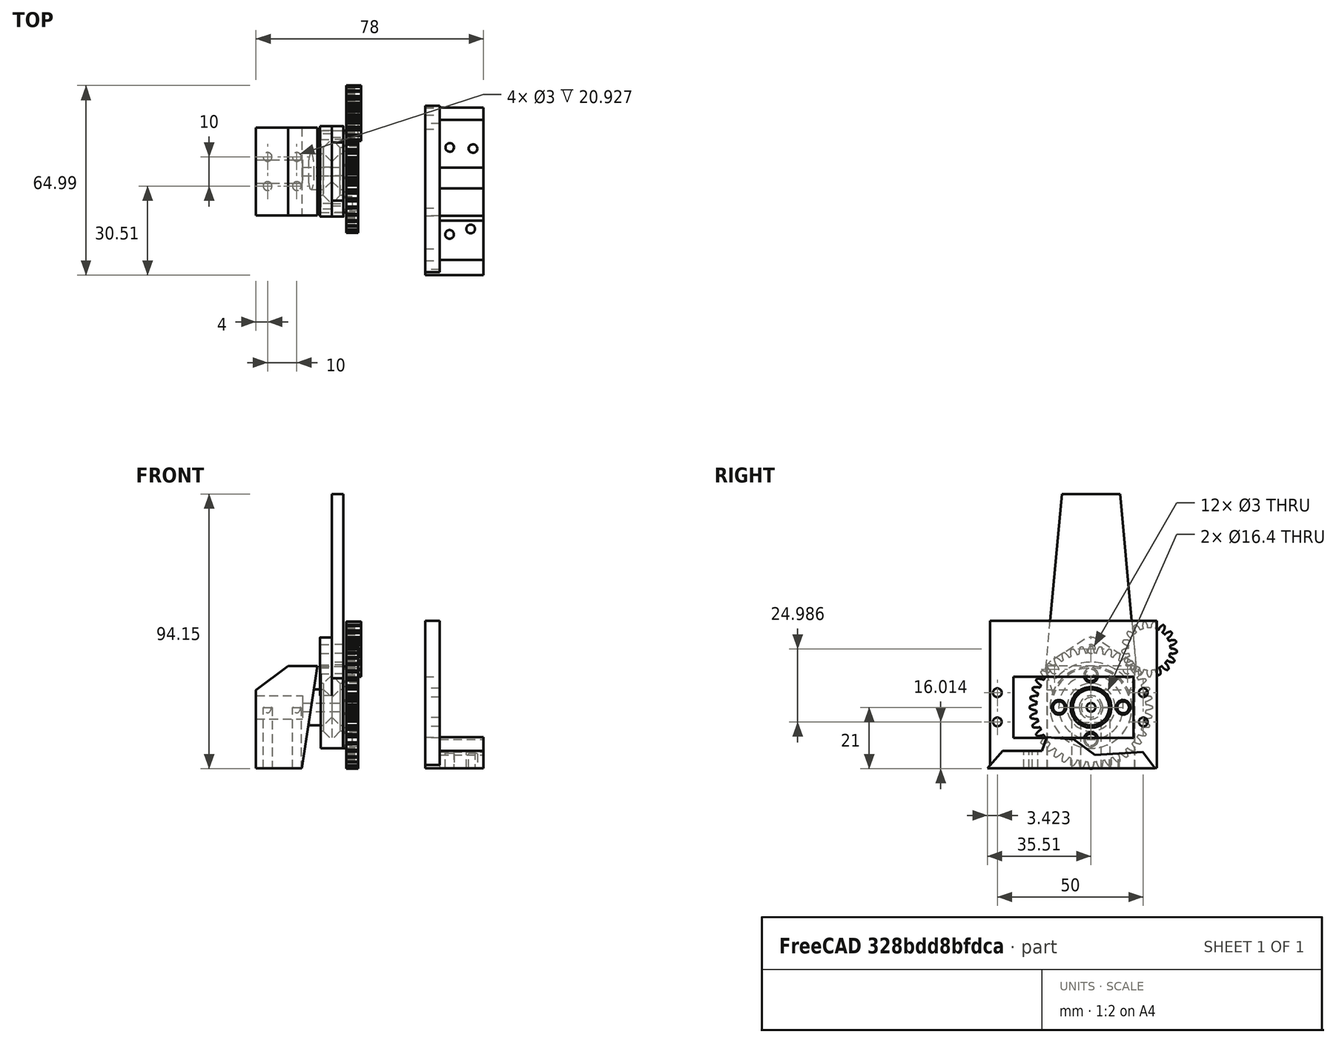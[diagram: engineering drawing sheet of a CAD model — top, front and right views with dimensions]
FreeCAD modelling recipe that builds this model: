
FCSTD DOCUMENT  (FreeCAD 0.16RUnknown)
Label: ArmV2
License: All rights reserved
LicenseURL: http://en.wikipedia.org/wiki/All_rights_reserved
objects: Sketcher::SketchObject×15, PartDesign::Pad×10, Part::Cut×5, PartDesign::Revolution×4, Part::MultiFuse×3, Part::FeaturePython×2, Mesh::Feature×2, Part::Cylinder×1
note: 54 computed .brp shape members not serialized (recipe doc carries the construction recipe); baked Part::Feature solids carry a one-line shape summary decoded from their .brp

FEATURE [Sketcher::SketchObject] Sketch
  Placement = pos=(0,0,0) rot=(-1,0,0;4.71239rad)
  sketch-geometry (22):
    g0: Circle [constr] CenterX=0 CenterY=7.20025 CenterZ=0 NormalX=0 NormalY=0 NormalZ=1 Radius=2.225
    g1: Circle [constr] CenterX=4.2322 CenterY=5.82513 CenterZ=0 NormalX=0 NormalY=0 NormalZ=1 Radius=2.225
    g2: Circle [constr] CenterX=0 CenterY=0 CenterZ=0 NormalX=0 NormalY=0 NormalZ=1 Radius=7.20025
    g3: LineSegment [constr] StartX=4.2322 StartY=5.82513 StartZ=0 EndX=0 EndY=0 EndZ=0
    g4: LineSegment StartX=0 StartY=11.054 StartZ=0 EndX=-2.85373 EndY=8.20025 EndZ=0
    g5: LineSegment StartX=-2.85373 StartY=8.20025 StartZ=0 EndX=-3.85373 EndY=8.20025 EndZ=0
    g6: LineSegment StartX=-3.85373 StartY=8.20025 StartZ=0 EndX=-3.85373 EndY=14.054 EndZ=0
    g7: LineSegment StartX=-3.85373 StartY=14.054 StartZ=0 EndX=3.85373 EndY=14.054 EndZ=0
    g8: LineSegment StartX=3.85373 StartY=14.054 StartZ=0 EndX=3.85373 EndY=8.20025 EndZ=0
    g9: LineSegment StartX=3.85373 StartY=8.20025 StartZ=0 EndX=2.85373 EndY=8.20025 EndZ=0
    g10: LineSegment StartX=2.85373 StartY=8.20025 StartZ=0 EndX=0 EndY=11.054 EndZ=0
    g11: Circle [constr] CenterX=0 CenterY=7.20025 CenterZ=0 NormalX=0 NormalY=0 NormalZ=1 Radius=2.725
    g12: LineSegment [constr] StartX=0 StartY=7.20025 StartZ=0 EndX=0 EndY=4.97525 EndZ=0
    g13: LineSegment [constr] StartX=0 StartY=4.97525 StartZ=0 EndX=0 EndY=4.47525 EndZ=0
    g14: GeomPoint [constr] X=0 Y=14.054 Z=0
    g15: LineSegment [constr] StartX=-3.85373 StartY=6.20025 StartZ=0 EndX=-2.85373 EndY=6.20025 EndZ=0
    g16: LineSegment [constr] StartX=-2.85373 StartY=6.20025 StartZ=0 EndX=0 EndY=3.34652 EndZ=0
    g17: LineSegment [constr] StartX=0 StartY=3.34652 StartZ=0 EndX=2.85373 EndY=6.20025 EndZ=0
    g18: LineSegment [constr] StartX=2.85373 StartY=6.20025 StartZ=0 EndX=3.85373 EndY=6.20025 EndZ=0
    g19: LineSegment [constr] StartX=3.85373 StartY=6.20025 StartZ=0 EndX=3.85373 EndY=0 EndZ=0
    g20: LineSegment [constr] StartX=3.85373 StartY=0 StartZ=0 EndX=-3.85373 EndY=0 EndZ=0
    g21: LineSegment [constr] StartX=-3.85373 StartY=0 StartZ=0 EndX=-3.85373 EndY=6.20025 EndZ=0
  constraints (62):
    c: PointOnObject(g0,g-2)
    c: Coincident(g2,g-1)
    c: PointOnObject(g0,g2)
    c: PointOnObject(g1,g2)
    c: Tangent(g0,g1)
    c: Equal(g1,g0)
    c: Radius(g0) = 2.225
    c: Coincident(g3,g1)
    c: Coincident(g3,g-1)
    c: Angle(g3,g-2) = 0.628319
    c: PointOnObject(g4,g-2)
    c: Coincident(g4,g5)
    c: Horizontal(g5)
    c: Coincident(g5,g6)
    c: Vertical(g6)
    c: Coincident(g6,g7)
    c: Horizontal(g7)
    c: Coincident(g7,g8)
    c: Vertical(g8)
    c: Coincident(g8,g9)
    c: Horizontal(g9)
    c: Coincident(g9,g10)
    c: Coincident(g10,g4)
    c: Coincident(g11,g0)
    c: Coincident(g12,g0)
    c: Coincident(g12,g13)
    c: PointOnObject(g12,g0)
    c: PointOnObject(g13,g11)
    c: Parallel(g13,g12)
    c: Distance(g13) = 0.5
    c: Tangent(g11,g4)
    c: Tangent(g10,g11)
    c: Equal(g4,g10)
    c: Equal(g9,g5)
    c: PointOnObject(g14,g7)
    c: PointOnObject(g14,g-2)
    c: DistanceY(g4,g14) = 3
    c: DistanceY(g0,g4) = 1
    c: DistanceX(g5,g5) = 1
    c: Angle(g4,g10) = 1.5708
    c: PointOnObject(g13,g-2)
    c: Coincident(g15,g16)
    c: Coincident(g16,g17)
    c: Coincident(g17,g18)
    c: Coincident(g18,g19)
    c: Coincident(g19,g20)
    c: Horizontal(g20)
    c: Coincident(g20,g21)
    c: Coincident(g21,g15)
    c: PointOnObject(g20,g-1)
    c: Vertical(g21)
    c: Vertical(g19)
    c: Horizontal(g18)
    c: Horizontal(g15)
    c: Equal(g18,g15)
    c: Equal(g15,g5)
    c: PointOnObject(g16,g-2)
    c: Tangent(g16,g11)
    c: Tangent(g11,g17)
    c: Angle(g17,g16) = 1.5708
    c: Equal(g16,g17)
    c: DistanceY(g15,g0) = 1
FEATURE [Sketcher::SketchObject] Sketch001
  Placement = pos=(0,0,0) rot=(1,0,0;1.5708rad)
  sketch-geometry (24):
    g0: Circle [constr] CenterX=0 CenterY=7.20025 CenterZ=0 NormalX=0 NormalY=0 NormalZ=1 Radius=2.225
    g1: Circle [constr] CenterX=4.2322 CenterY=5.82513 CenterZ=0 NormalX=0 NormalY=0 NormalZ=1 Radius=2.225
    g2: Circle [constr] CenterX=0 CenterY=0 CenterZ=0 NormalX=0 NormalY=0 NormalZ=1 Radius=7.20025
    g3: LineSegment [constr] StartX=4.2322 StartY=5.82513 StartZ=0 EndX=0 EndY=0 EndZ=0
    g4: LineSegment [constr] StartX=0 StartY=11.054 StartZ=0 EndX=-2.85373 EndY=8.20025 EndZ=0
    g5: LineSegment [constr] StartX=-2.85373 StartY=8.20025 StartZ=0 EndX=-7.85373 EndY=8.20025 EndZ=0
    g6: LineSegment [constr] StartX=-7.85373 StartY=8.20025 StartZ=0 EndX=-7.85373 EndY=14.054 EndZ=0
    g7: LineSegment [constr] StartX=-7.85373 StartY=14.054 StartZ=0 EndX=7.85373 EndY=14.054 EndZ=0
    g8: LineSegment [constr] StartX=7.85373 StartY=14.054 StartZ=0 EndX=7.85373 EndY=8.20025 EndZ=0
    g9: LineSegment [constr] StartX=7.85373 StartY=8.20025 StartZ=0 EndX=2.85373 EndY=8.20025 EndZ=0
    g10: LineSegment [constr] StartX=2.85373 StartY=8.20025 StartZ=0 EndX=0 EndY=11.054 EndZ=0
    g11: Circle [constr] CenterX=0 CenterY=7.20025 CenterZ=0 NormalX=0 NormalY=0 NormalZ=1 Radius=2.725
    g12: LineSegment [constr] StartX=0 StartY=7.20025 StartZ=0 EndX=0 EndY=4.97525 EndZ=0
    g13: LineSegment [constr] StartX=0 StartY=4.97525 StartZ=0 EndX=0 EndY=4.47525 EndZ=0
    g14: GeomPoint [constr] X=0 Y=14.054 Z=0
    g15: LineSegment StartX=-7.85373 StartY=6.20025 StartZ=0 EndX=-2.85373 EndY=6.20025 EndZ=0
    g16: LineSegment StartX=-2.85373 StartY=6.20025 StartZ=0 EndX=0 EndY=3.34652 EndZ=0
    g17: LineSegment [constr] StartX=0 StartY=3.34652 StartZ=0 EndX=2.85373 EndY=6.20025 EndZ=0
    g18: LineSegment [constr] StartX=2.85373 StartY=6.20025 StartZ=0 EndX=7.85373 EndY=6.20025 EndZ=0
    g19: LineSegment [constr] StartX=7.85373 StartY=6.20025 StartZ=0 EndX=7.85373 EndY=0 EndZ=0
    g20: LineSegment StartX=-7.85373 StartY=0 StartZ=0 EndX=-7.85373 EndY=6.20025 EndZ=0
    g21: LineSegment StartX=0 StartY=3.34652 StartZ=0 EndX=0 EndY=0 EndZ=0
    g22: LineSegment StartX=-7.85373 StartY=0 StartZ=0 EndX=0 EndY=0 EndZ=0
    g23: LineSegment [constr] StartX=0 StartY=0 StartZ=0 EndX=7.85373 EndY=0 EndZ=0
  constraints (66):
    c: PointOnObject(g0,g-2)
    c: Coincident(g2,g-1)
    c: PointOnObject(g0,g2)
    c: PointOnObject(g1,g2)
    c: Tangent(g0,g1)
    c: Equal(g1,g0)
    c: Radius(g0) = 2.225
    c: Coincident(g3,g1)
    c: Coincident(g3,g-1)
    c: Angle(g3,g-2) = 0.628319
    c: PointOnObject(g4,g-2)
    c: Coincident(g4,g5)
    c: Horizontal(g5)
    c: Coincident(g5,g6)
    c: Vertical(g6)
    c: Coincident(g6,g7)
    c: Horizontal(g7)
    c: Coincident(g7,g8)
    c: Vertical(g8)
    c: Coincident(g8,g9)
    c: Horizontal(g9)
    c: Coincident(g9,g10)
    c: Coincident(g10,g4)
    c: Coincident(g11,g0)
    c: Coincident(g12,g0)
    c: Coincident(g12,g13)
    c: PointOnObject(g12,g0)
    c: PointOnObject(g13,g11)
    c: Parallel(g13,g12)
    c: Distance(g13) = 0.5
    c: Tangent(g11,g4)
    c: Tangent(g10,g11)
    c: Equal(g4,g10)
    c: Equal(g9,g5)
    c: PointOnObject(g14,g7)
    c: PointOnObject(g14,g-2)
    c: DistanceY(g4,g14) = 3
    c: DistanceY(g0,g4) = 1
    c: DistanceX(g5,g5) = 5
    c: Angle(g4,g10) = 1.5708
    c: PointOnObject(g13,g-2)
    c: Coincident(g15,g16)
    c: Coincident(g16,g17)
    c: Coincident(g17,g18)
    c: Coincident(g18,g19)
    c: Coincident(g20,g15)
    c: PointOnObject(g20,g-1)
    c: Vertical(g20)
    c: Vertical(g19)
    c: Horizontal(g18)
    c: Horizontal(g15)
    c: Equal(g18,g15)
    c: Equal(g15,g5)
    c: PointOnObject(g16,g-2)
    c: Tangent(g16,g11)
    c: Tangent(g11,g17)
    c: Angle(g17,g16) = 1.5708
    c: Equal(g16,g17)
    c: DistanceY(g15,g0) = 1
    c: Coincident(g21,g16)
    c: Coincident(g20,g22)
    c: Coincident(g22,g21)
    c: Coincident(g22,g23)
    c: Coincident(g23,g19)
    c: Coincident(g-1,g21)
    c: PointOnObject(g19,g-1)
FEATURE [PartDesign::Revolution] Revolution  label="OuterRace"
  Angle = 360
  Axis = (1,0,0)
  Base = (0,0,0)
  Placement = pos=(0,0,0) rot=(-1,0,0;4.71239rad)
  ReferenceAxis = -> Sketch [H_Axis]
  Sketch = -> Sketch
FEATURE [PartDesign::Revolution] Revolution001  label="InnerRace002"
  Angle = 360
  Axis = (1,0,0)
  Base = (0,0,0)
  Placement = pos=(0,0,0) rot=(1,0,0;1.5708rad)
  ReferenceAxis = -> Sketch001 [H_Axis]
  Sketch = -> Sketch001
FEATURE [Sketcher::SketchObject] Sketch002
  Placement = pos=(0,0,0) rot=(1,0,0;1.5708rad)
  sketch-geometry (24):
    g0: Circle [constr] CenterX=0 CenterY=7.20025 CenterZ=0 NormalX=0 NormalY=0 NormalZ=1 Radius=2.225
    g1: Circle [constr] CenterX=4.2322 CenterY=5.82513 CenterZ=0 NormalX=0 NormalY=0 NormalZ=1 Radius=2.225
    g2: Circle [constr] CenterX=0 CenterY=0 CenterZ=0 NormalX=0 NormalY=0 NormalZ=1 Radius=7.20025
    g3: LineSegment [constr] StartX=4.2322 StartY=5.82513 StartZ=0 EndX=0 EndY=0 EndZ=0
    g4: LineSegment [constr] StartX=0 StartY=11.054 StartZ=0 EndX=-2.85373 EndY=8.20025 EndZ=0
    g5: LineSegment [constr] StartX=-2.85373 StartY=8.20025 StartZ=0 EndX=-3.85373 EndY=8.20025 EndZ=0
    g6: LineSegment [constr] StartX=-3.85373 StartY=8.20025 StartZ=0 EndX=-3.85373 EndY=14.054 EndZ=0
    g7: LineSegment [constr] StartX=-3.85373 StartY=14.054 StartZ=0 EndX=3.85373 EndY=14.054 EndZ=0
    g8: LineSegment [constr] StartX=3.85373 StartY=14.054 StartZ=0 EndX=3.85373 EndY=8.20025 EndZ=0
    g9: LineSegment [constr] StartX=3.85373 StartY=8.20025 StartZ=0 EndX=2.85373 EndY=8.20025 EndZ=0
    g10: LineSegment [constr] StartX=2.85373 StartY=8.20025 StartZ=0 EndX=0 EndY=11.054 EndZ=0
    g11: Circle [constr] CenterX=0 CenterY=7.20025 CenterZ=0 NormalX=0 NormalY=0 NormalZ=1 Radius=2.725
    g12: LineSegment [constr] StartX=0 StartY=7.20025 StartZ=0 EndX=0 EndY=4.97525 EndZ=0
    g13: LineSegment [constr] StartX=0 StartY=4.97525 StartZ=0 EndX=0 EndY=4.47525 EndZ=0
    g14: GeomPoint [constr] X=0 Y=14.054 Z=0
    g15: LineSegment [constr] StartX=-3.85373 StartY=6.20025 StartZ=0 EndX=-2.85373 EndY=6.20025 EndZ=0
    g16: LineSegment [constr] StartX=-2.85373 StartY=6.20025 StartZ=0 EndX=0 EndY=3.34652 EndZ=0
    g17: LineSegment StartX=0 StartY=3.34652 StartZ=0 EndX=2.85373 EndY=6.20025 EndZ=0
    g18: LineSegment StartX=2.85373 StartY=6.20025 StartZ=0 EndX=3.85373 EndY=6.20025 EndZ=0
    g19: LineSegment StartX=3.85373 StartY=6.20025 StartZ=0 EndX=3.85373 EndY=0 EndZ=0
    g20: LineSegment [constr] StartX=-3.85373 StartY=0 StartZ=0 EndX=-3.85373 EndY=6.20025 EndZ=0
    g21: LineSegment StartX=0 StartY=3.34652 StartZ=0 EndX=0 EndY=0 EndZ=0
    g22: LineSegment [constr] StartX=-3.85373 StartY=0 StartZ=0 EndX=0 EndY=0 EndZ=0
    g23: LineSegment StartX=0 StartY=0 StartZ=0 EndX=3.85373 EndY=0 EndZ=0
  constraints (66):
    c: PointOnObject(g0,g-2)
    c: Coincident(g2,g-1)
    c: PointOnObject(g0,g2)
    c: PointOnObject(g1,g2)
    c: Tangent(g0,g1)
    c: Equal(g1,g0)
    c: Radius(g0) = 2.225
    c: Coincident(g3,g1)
    c: Coincident(g3,g-1)
    c: Angle(g3,g-2) = 0.628319
    c: PointOnObject(g4,g-2)
    c: Coincident(g4,g5)
    c: Horizontal(g5)
    c: Coincident(g5,g6)
    c: Vertical(g6)
    c: Coincident(g6,g7)
    c: Horizontal(g7)
    c: Coincident(g7,g8)
    c: Vertical(g8)
    c: Coincident(g8,g9)
    c: Horizontal(g9)
    c: Coincident(g9,g10)
    c: Coincident(g10,g4)
    c: Coincident(g11,g0)
    c: Coincident(g12,g0)
    c: Coincident(g12,g13)
    c: PointOnObject(g12,g0)
    c: PointOnObject(g13,g11)
    c: Parallel(g13,g12)
    c: Distance(g13) = 0.5
    c: Tangent(g11,g4)
    c: Tangent(g10,g11)
    c: Equal(g4,g10)
    c: Equal(g9,g5)
    c: PointOnObject(g14,g7)
    c: PointOnObject(g14,g-2)
    c: DistanceY(g4,g14) = 3
    c: DistanceY(g0,g4) = 1
    c: DistanceX(g5,g5) = 1
    c: Angle(g4,g10) = 1.5708
    c: PointOnObject(g13,g-2)
    c: Coincident(g15,g16)
    c: Coincident(g16,g17)
    c: Coincident(g17,g18)
    c: Coincident(g18,g19)
    c: Coincident(g20,g15)
    c: PointOnObject(g20,g-1)
    c: Vertical(g20)
    c: Vertical(g19)
    c: Horizontal(g18)
    c: Horizontal(g15)
    c: Equal(g18,g15)
    c: Equal(g15,g5)
    c: PointOnObject(g16,g-2)
    c: Tangent(g16,g11)
    c: Tangent(g11,g17)
    c: Angle(g17,g16) = 1.5708
    c: Equal(g16,g17)
    c: DistanceY(g15,g0) = 1
    c: Coincident(g21,g16)
    c: Coincident(g20,g22)
    c: Coincident(g22,g21)
    c: Coincident(g22,g23)
    c: Coincident(g23,g19)
    c: Coincident(g-1,g21)
    c: PointOnObject(g19,g-1)
FEATURE [PartDesign::Revolution] Revolution002  label="InnerRace"
  Angle = 360
  Axis = (1,0,0)
  Base = (0,0,0)
  Placement = pos=(0,0,0) rot=(1,0,0;1.5708rad)
  ReferenceAxis = -> Sketch002 [H_Axis]
  Sketch = -> Sketch002
FEATURE [Sketcher::SketchObject] Sketch003
  sketch-geometry (5):
    g0: Circle CenterX=-22 CenterY=5 CenterZ=0 NormalX=0 NormalY=0 NormalZ=1 Radius=1.5
    g1: Circle CenterX=-12 CenterY=5 CenterZ=0 NormalX=0 NormalY=0 NormalZ=1 Radius=1.5
    g2: Circle CenterX=-22 CenterY=-5 CenterZ=0 NormalX=0 NormalY=0 NormalZ=1 Radius=1.5
    g3: Circle CenterX=-12 CenterY=-5 CenterZ=0 NormalX=0 NormalY=0 NormalZ=1 Radius=1.5
    g4: LineSegment [constr] StartX=-22 StartY=5 StartZ=0 EndX=-12 EndY=5 EndZ=0
  constraints (12):
    c: Equal(g0,g1)
    c: Equal(g1,g3)
    c: Equal(g3,g2)
    c: Radius(g1) = 1.5
    c: Symmetric(g1,g3,g-1)
    c: Symmetric(g0,g2,g-1)
    c: DistanceY(g3,g1) = 10
    c: DistanceX(g0,g1) = 10
    c: Coincident(g4,g0)
    c: Coincident(g4,g1)
    c: Horizontal(g4)
    c: DistanceX(g1,g-1) = 12
FEATURE [PartDesign::Pad] Pad  label="MountingCutouts"
  Length = 50
  Length2 = 100
  Reversed = true
  Sketch = -> Sketch003
  Type = 0
FEATURE [Sketcher::SketchObject] Sketch004
  Placement = pos=(0,0,0) rot=(-1,0,0;4.71239rad)
  sketch-geometry (5):
    g0: LineSegment StartX=-26 StartY=-20.9274 StartZ=0 EndX=-26 EndY=5.97558 EndZ=0
    g1: LineSegment StartX=-26 StartY=5.97558 StartZ=0 EndX=-14.9603 EndY=14.1062 EndZ=0
    g2: LineSegment StartX=-14.9603 StartY=14.1062 StartZ=0 EndX=-4.9664 EndY=14.1062 EndZ=0
    g3: LineSegment StartX=-4.9664 StartY=14.1062 StartZ=0 EndX=-10.2402 EndY=-20.9274 EndZ=0
    g4: LineSegment StartX=-10.2402 StartY=-20.9274 StartZ=0 EndX=-26 EndY=-20.9274 EndZ=0
  constraints (9):
    c: Vertical(g0)
    c: Coincident(g0,g1)
    c: Coincident(g1,g2)
    c: Horizontal(g2)
    c: Coincident(g2,g3)
    c: Coincident(g4,g0)
    c: Horizontal(g4)
    c: Coincident(g3,g4)
    c: DistanceX(g0,g-1) = 26
FEATURE [PartDesign::Pad] Pad001
  Length = 30
  Length2 = 100
  Midplane = true
  Placement = pos=(0,0,0) rot=(-1,0,0;4.71239rad)
  Sketch = -> Sketch004
  Type = 0
FEATURE [Part::MultiFuse] Fusion  label="Base"
  Shapes = -> [Pad001,Revolution001]
FEATURE [Sketcher::SketchObject] Sketch005
  Placement = pos=(0,0,0) rot=(0.57735,0.57735,0.57735;2.0944rad)
  sketch-geometry (11):
    g0: Circle CenterX=12.5 CenterY=13 CenterZ=0 NormalX=0 NormalY=0 NormalZ=1 Radius=1.5
    g1: Circle CenterX=-12.5 CenterY=13 CenterZ=0 NormalX=0 NormalY=0 NormalZ=1 Radius=1.5
    g2: ArcOfCircle CenterX=12.5 CenterY=13 CenterZ=0 NormalX=0 NormalY=0 NormalZ=1 Radius=3 StartAngle=5.98741 EndAngle=7.27364
    g3: ArcOfCircle CenterX=-12.5 CenterY=13 CenterZ=0 NormalX=0 NormalY=0 NormalZ=1 Radius=3 StartAngle=2.15114 EndAngle=3.43736
    g4: ArcOfCircle CenterX=0 CenterY=0 CenterZ=0 NormalX=0 NormalY=0 NormalZ=1 Radius=13.5 StartAngle=0.300812 EndAngle=2.84078
    g5: LineSegment StartX=12.8938 StartY=4 StartZ=0 EndX=15.3697 EndY=12.1256 EndZ=0
    g6: LineSegment StartX=-15.3697 StartY=12.1256 StartZ=0 EndX=-12.8938 EndY=4 EndZ=0
    g7: Circle CenterX=0 CenterY=20 CenterZ=0 NormalX=0 NormalY=0 NormalZ=1 Radius=1.5
    g8: LineSegment StartX=14.1449 StartY=15.5088 StartZ=0 EndX=2.19327 EndY=23.3451 EndZ=0
    g9: LineSegment StartX=-2.19327 StartY=23.3451 StartZ=0 EndX=-14.1449 EndY=15.5088 EndZ=0
    g10: ArcOfCircle CenterX=0 CenterY=20 CenterZ=0 NormalX=0 NormalY=0 NormalZ=1 Radius=4 StartAngle=0.990444 EndAngle=2.15115
  constraints (31):
    c: Radius(g1) = 1.5
    c: Equal(g1,g0)
    c: Symmetric(g0,g1,g-2)
    c: DistanceX(g1,g0) = 25
    c: Coincident(g2,g0)
    c: Coincident(g3,g1)
    c: Coincident(g4,g-1)
    c: Coincident(g5,g4)
    c: Coincident(g5,g2)
    c: Coincident(g6,g3)
    c: Coincident(g6,g4)
    c: Tangent(g6,g3)
    c: Radius(g2) = 3
    c: Equal(g2,g3)
    c: Tangent(g2,g5)
    c: Radius(g4) = 13.5
    c: Symmetric(g4,g4,g-2)
    c: DistanceY(g-1,g4) = 4
    c: DistanceY(g-1,g1) = 13
    c: PointOnObject(g7,g-2)
    c: Equal(g7,g0)
    c: Tangent(g2,g8) = -1.5708
    c: Coincident(g9,g3)
    c: Tangent(g3,g9)
    c: Coincident(g10,g7)
    c: Coincident(g10,g9)
    c: Coincident(g10,g8)
    c: Tangent(g10,g8)
    c: Tangent(g10,g9)
    c: Radius(g10) = 4
    c: DistanceY(g-1,g7) = 20
FEATURE [PartDesign::Pad] Pad002  label="ArmMountPad"
  Length = 4
  Length2 = 100
  Placement = pos=(0,0,0) rot=(0.57735,0.57735,0.57735;2.0944rad)
  Reversed = true
  Sketch = -> Sketch005
  Type = 0
FEATURE [Part::FeaturePython] InvoluteGear  label="Gear"  # WARN: FeaturePython — macro-defined, semantics opaque (R4)
  Placement = pos=(4,0,0) rot=(0,1,0;1.5708rad)
  backlash = 0
  beta = 0
  clearance = 0.25
  height = 5
  module = 1
  numpoints = 6
  pressure_angle = 20
  shift = 0
  simple = false
  teeth = 40
  undercut = false
FEATURE [Sketcher::SketchObject] Sketch006
  Placement = pos=(0,0,0) rot=(0.57735,0.57735,0.57735;2.0944rad)
  sketch-geometry (6):
    g0: Circle CenterX=0 CenterY=0 CenterZ=0 NormalX=0 NormalY=0 NormalZ=1 Radius=7
    g1: Circle CenterX=0 CenterY=11 CenterZ=0 NormalX=0 NormalY=0 NormalZ=1 Radius=2.5
    g2: Circle CenterX=0 CenterY=-11 CenterZ=0 NormalX=0 NormalY=0 NormalZ=1 Radius=2.5
    g3: Circle CenterX=11 CenterY=0 CenterZ=0 NormalX=0 NormalY=0 NormalZ=1 Radius=2.5
    g4: Circle CenterX=-11 CenterY=0 CenterZ=0 NormalX=0 NormalY=0 NormalZ=1 Radius=2.5
    g5: Circle [constr] CenterX=0 CenterY=0 CenterZ=0 NormalX=0 NormalY=0 NormalZ=1 Radius=11
  constraints (16):
    c: Coincident(g0,g-1)
    c: Radius(g0) = 7
    c: PointOnObject(g1,g-2)
    c: PointOnObject(g2,g-2)
    c: PointOnObject(g3,g-1)
    c: PointOnObject(g4,g-1)
    c: Coincident(g5,g-1)
    c: PointOnObject(g1,g5)
    c: PointOnObject(g4,g5)
    c: PointOnObject(g2,g5)
    c: PointOnObject(g3,g5)
    c: Radius(g3) = 2.5
    c: Equal(g3,g2)
    c: Equal(g3,g4)
    c: Equal(g3,g1)
    c: Radius(g5) = 11
FEATURE [PartDesign::Pad] Pad003  label="CenterCutout"
  Length = 50
  Length2 = 100
  Midplane = true
  Placement = pos=(0,0,0) rot=(0.57735,0.57735,0.57735;2.0944rad)
  Sketch = -> Sketch006
  Type = 0
FEATURE [Part::Cut] Cut  label="GearRing"
  Base = -> InvoluteGear
  Tool = -> Pad003
FEATURE [Mesh::Feature] ParallaxServo
  Placement = pos=(58,10,0) rot=(0.579113,-0.576467,-0.576467;2.0944rad)
FEATURE [Sketcher::SketchObject] Sketch007
  Placement = pos=(0,0,0) rot=(-1,0,0;4.71239rad)
  sketch-geometry (6):
    g0: LineSegment StartX=-35 StartY=0 StartZ=0 EndX=-35 EndY=4 EndZ=0
    g1: LineSegment StartX=-35 StartY=4 StartZ=0 EndX=-10 EndY=4 EndZ=0
    g2: LineSegment StartX=-10 StartY=4 StartZ=0 EndX=-10 EndY=1.5 EndZ=0
    g3: LineSegment StartX=-10 StartY=1.5 StartZ=0 EndX=0 EndY=1.5 EndZ=0
    g4: LineSegment StartX=0 StartY=1.5 StartZ=0 EndX=0 EndY=0 EndZ=0
    g5: LineSegment StartX=0 StartY=0 StartZ=0 EndX=-35 EndY=0 EndZ=0
  constraints (18):
    c: PointOnObject(g0,g-1)
    c: Vertical(g0)
    c: Coincident(g0,g1)
    c: Horizontal(g1)
    c: Coincident(g1,g2)
    c: Vertical(g2)
    c: Coincident(g2,g3)
    c: Horizontal(g3)
    c: Coincident(g3,g4)
    c: PointOnObject(g4,g-1)
    c: Coincident(g4,g5)
    c: Coincident(g5,g0)
    c: Vertical(g4)
    c: DistanceX(g2,g-1) = 10
    c: Distance(g4) = 1.5
    c: DistanceY(g4,g1) = 4
    c: Coincident(g4,g-1)
    c: DistanceX(g1,g1) = 25
FEATURE [PartDesign::Revolution] Revolution003  label="BearingMountCutout"
  Angle = 360
  Axis = (1,0,0)
  Base = (0,0,0)
  Placement = pos=(0,0,0) rot=(-1,0,0;4.71239rad)
  ReferenceAxis = -> Sketch007 [H_Axis]
  Sketch = -> Sketch007
FEATURE [Part::MultiFuse] Fusion001  label="Cutouts"
  Shapes = -> [Pad,Revolution003]
FEATURE [Part::Cut] Cut001  label="Base001"
  Base = -> Fusion
  Tool = -> Fusion001
FEATURE [Part::Cylinder] Cylinder  label="ScrewCutout"
  Angle = 360
  Height = 10
  Placement = pos=(0,0,0) rot=(0,1,0;1.5708rad)
  Radius = 1.5
FEATURE [Part::Cut] Cut002  label="InnerRace001"
  Base = -> Revolution002
  Tool = -> Cylinder
FEATURE [Sketcher::SketchObject] Sketch008
  Placement = pos=(32,0,0) rot=(0.57735,0.57735,0.57735;2.0944rad)
  sketch-geometry (18):
    g0: LineSegment StartX=-34.5361 StartY=29.689 StartZ=0 EndX=22.5251 EndY=29.689 EndZ=0
    g1: LineSegment StartX=22.5251 StartY=29.689 StartZ=0 EndX=22.5251 EndY=-20.7193 EndZ=0
    g2: LineSegment StartX=22.5251 StartY=-20.7193 StartZ=0 EndX=-34.5361 EndY=-20.7193 EndZ=0
    g3: LineSegment StartX=-34.5361 StartY=-20.7193 StartZ=0 EndX=-34.5361 EndY=29.689 EndZ=0
    g4: LineSegment StartX=-26.5361 StartY=10.4396 StartZ=0 EndX=14.5251 EndY=10.4396 EndZ=0
    g5: LineSegment StartX=14.5251 StartY=10.4396 StartZ=0 EndX=14.5251 EndY=-10.4396 EndZ=0
    g6: LineSegment StartX=14.5251 StartY=-10.4396 StartZ=0 EndX=-26.5361 EndY=-10.4396 EndZ=0
    g7: LineSegment StartX=-26.5361 StartY=-10.4396 StartZ=0 EndX=-26.5361 EndY=10.4396 EndZ=0
    g8: Circle CenterX=-32.0873 CenterY=5.01347 CenterZ=0 NormalX=0 NormalY=0 NormalZ=1 Radius=1.5
    g9: Circle CenterX=-32.0873 CenterY=-4.98653 CenterZ=0 NormalX=0 NormalY=0 NormalZ=1 Radius=1.5
    g10: Circle CenterX=17.9127 CenterY=5.01347 CenterZ=0 NormalX=0 NormalY=0 NormalZ=1 Radius=1.5
    g11: Circle CenterX=17.9127 CenterY=-4.98653 CenterZ=0 NormalX=0 NormalY=0 NormalZ=1 Radius=1.5
    g12: LineSegment [constr] StartX=-32.0873 StartY=5.01347 StartZ=0 EndX=17.9127 EndY=5.01347 EndZ=0
    g13: LineSegment [constr] StartX=17.9127 StartY=5.01347 StartZ=0 EndX=17.9127 EndY=-4.98653 EndZ=0
    g14: LineSegment [constr] StartX=17.9127 StartY=-4.98653 StartZ=0 EndX=-32.0873 EndY=-4.98653 EndZ=0
    g15: LineSegment [constr] StartX=-32.0873 StartY=-4.98653 StartZ=0 EndX=-32.0873 EndY=5.01347 EndZ=0
    g16: LineSegment [constr] StartX=-34.5361 StartY=29.689 StartZ=0 EndX=-26.5361 EndY=10.4396 EndZ=0
    g17: LineSegment [constr] StartX=14.5251 StartY=10.4396 StartZ=0 EndX=22.5251 EndY=29.689 EndZ=0
  constraints (41):
    c: Coincident(g0,g1)
    c: Coincident(g1,g2)
    c: Coincident(g2,g3)
    c: Coincident(g3,g0)
    c: Horizontal(g0)
    c: Horizontal(g2)
    c: Vertical(g1)
    c: Vertical(g3)
    c: Coincident(g4,g5)
    c: Coincident(g5,g6)
    c: Coincident(g6,g7)
    c: Coincident(g7,g4)
    c: Horizontal(g4)
    c: Horizontal(g6)
    c: Vertical(g5)
    c: Vertical(g7)
    c: Radius(g10) = 1.5  'Blarg'
    c: Equal(g10,g11)
    c: Equal(g10,g9)
    c: Equal(g10,g8)
    c: Symmetric(g4,g5,g-1)
    c: Coincident(g12,g13)
    c: Coincident(g13,g14)
    c: Coincident(g14,g15)
    c: Coincident(g15,g12)
    c: Horizontal(g12)
    c: Horizontal(g14)
    c: Vertical(g13)
    c: Vertical(g15)
    c: Coincident(g12,g8)
    c: Coincident(g13,g11)
    c: Coincident(g10,g12)
    c: Coincident(g9,g14)
    c: DistanceY(g15,g15) = 10
    c: DistanceX(g12,g12) = 50
    c: Coincident(g16,g0)
    c: Coincident(g16,g4)
    c: Coincident(g17,g4)
    c: Coincident(g17,g0)
    c: Equal(g17,g16)
    c: DistanceX(g4,g0) = 8
FEATURE [PartDesign::Pad] Pad004  label="ServoMountPlate"
  Length = 5
  Length2 = 100
  Placement = pos=(32,0,0) rot=(0.57735,0.57735,0.57735;2.0944rad)
  Sketch = -> Sketch008
  Type = 0
FEATURE [Sketcher::SketchObject] Sketch009
  Placement = pos=(32,0,0) rot=(0.57735,0.57735,0.57735;2.0944rad)
  sketch-geometry (8):
    g0: LineSegment StartX=-35.5083 StartY=-20.8508 StartZ=0 EndX=-30.3219 EndY=-14.9351 EndZ=0
    g1: LineSegment StartX=-30.3219 StartY=-14.9351 StartZ=0 EndX=-16.7886 EndY=-14.9351 EndZ=0
    g2: LineSegment StartX=-16.7886 StartY=-14.9351 StartZ=0 EndX=-15.1679 EndY=-10.2349 EndZ=0
    g3: LineSegment StartX=-15.1679 StartY=-10.2349 StartZ=0 EndX=-5.84857 EndY=-10.9642 EndZ=0
    g4: LineSegment StartX=-5.84857 StartY=-10.9642 StartZ=0 EndX=1.36377 EndY=-16.3127 EndZ=0
    g5: LineSegment StartX=1.36377 StartY=-16.3127 StartZ=0 EndX=17.7333 EndY=-15.2592 EndZ=0
    g6: LineSegment StartX=17.7333 StartY=-15.2592 StartZ=0 EndX=21.8663 EndY=-20.8508 EndZ=0
    g7: LineSegment StartX=21.8663 StartY=-20.8508 StartZ=0 EndX=-35.5083 EndY=-20.8508 EndZ=0
  constraints (10):
    c: Coincident(g0,g1)
    c: Horizontal(g1)
    c: Coincident(g1,g2)
    c: Coincident(g2,g3)
    c: Coincident(g3,g4)
    c: Coincident(g4,g5)
    c: Coincident(g5,g6)
    c: Coincident(g6,g7)
    c: Coincident(g7,g0)
    c: Horizontal(g7)
FEATURE [PartDesign::Pad] Pad005  label="MountSupportPad"
  Length = 20
  Length2 = 100
  Placement = pos=(32,0,0) rot=(0.57735,0.57735,0.57735;2.0944rad)
  Sketch = -> Sketch009
  Type = 0
FEATURE [Sketcher::SketchObject] Sketch010
  sketch-geometry (4):
    g0: Circle CenterX=40.4291 CenterY=8.26343 CenterZ=0 NormalX=0 NormalY=0 NormalZ=1 Radius=1.5
    g1: Circle CenterX=48.3707 CenterY=7.85824 CenterZ=0 NormalX=0 NormalY=0 NormalZ=1 Radius=1.5
    g2: Circle CenterX=40.348 CenterY=-21.5584 CenterZ=0 NormalX=0 NormalY=0 NormalZ=1 Radius=1.5
    g3: Circle CenterX=47.5604 CenterY=-19.6945 CenterZ=0 NormalX=0 NormalY=0 NormalZ=1 Radius=1.5
  constraints (4):
    c: Radius(g0) = 1.5
    c: Equal(g0,g1)
    c: Equal(g0,g2)
    c: Equal(g0,g3)
FEATURE [PartDesign::Pad] Pad006  label="ScrewCutouts"
  Length = 100
  Length2 = 100
  Reversed = true
  Sketch = -> Sketch010
  Type = 0
FEATURE [Part::MultiFuse] Fusion003
  Shapes = -> [Pad004,Pad005]
FEATURE [Part::Cut] Cut003
  Base = -> Fusion003
  Tool = -> Pad006
FEATURE [Mesh::Feature] ParallaxServo001
  Placement = pos=(58,10,20) rot=(-0.578621,-0.578621,0.574801;2.0944rad)
FEATURE [Part::FeaturePython] InvoluteGear002  label="Gear002"  # WARN: FeaturePython — macro-defined, semantics opaque (R4)
  Placement = pos=(5,20,20) rot=(0,1,0;1.5708rad)
  backlash = 0
  beta = 0
  clearance = 0.25
  height = 5
  module = 1
  numpoints = 6
  pressure_angle = 20
  shift = 0
  simple = false
  teeth = 17
  undercut = false
FEATURE [Sketcher::SketchObject] Sketch011
  Placement = pos=(-6.93278,0,1.04363) rot=(0.604027,0.604027,0.519906;2.1827rad)
  Support = -> Cut001 [Face7]
  sketch-geometry (6):
    g0: GeomPoint [constr] X=-61.677 Y=90.0473 Z=0
    g1: LineSegment StartX=-61.677 StartY=90.0473 StartZ=0 EndX=-33.5301 EndY=122.647 EndZ=0
    g2: LineSegment StartX=-33.5301 StartY=122.647 StartZ=0 EndX=-75.8934 EndY=130.413 EndZ=0
    g3: LineSegment StartX=-33.5301 StartY=122.647 StartZ=0 EndX=-24.385 EndY=130.53 EndZ=0
    g4: LineSegment StartX=-83.167 StartY=100.919 StartZ=0 EndX=-87.3473 EndY=112.246 EndZ=0
    g5: LineSegment StartX=-87.3473 StartY=112.246 StartZ=0 EndX=-24.385 EndY=130.53 EndZ=0
  constraints (15):
    c: DistanceX(g0) = -61.677
    c: DistanceY(g0) = 90.0473
    c: Coincident(g1,g0)
    c: Coincident(g2,g1)
    c: Equal(g2,g1)
    c: Distance(g2) = 43.0693
    c: Coincident(g3,g1)
    c: Angle(g3,g2) = 2.24887
    c: Coincident(g5,g4)
    c: Coincident(g5,g3)
    c: DistanceX(g4) = -83.167
    c: DistanceY(g4) = 100.919
    c: Equal(g4,g3)
    c: Distance(g4) = 12.0737
    c: Distance(g5) = 65.5633
FEATURE [Sketcher::SketchObject] Sketch012
  Placement = pos=(4,0,0) rot=(0.57735,0.57735,0.57735;2.0944rad)
  sketch-geometry (5):
    g0: Circle CenterX=0 CenterY=11 CenterZ=0 NormalX=0 NormalY=0 NormalZ=1 Radius=2
    g1: Circle CenterX=0 CenterY=-11 CenterZ=0 NormalX=0 NormalY=0 NormalZ=1 Radius=2
    g2: Circle CenterX=11 CenterY=0 CenterZ=0 NormalX=0 NormalY=0 NormalZ=1 Radius=2
    g3: Circle CenterX=-11 CenterY=0 CenterZ=0 NormalX=0 NormalY=0 NormalZ=1 Radius=2
    g4: Circle [constr] CenterX=0 CenterY=0 CenterZ=0 NormalX=0 NormalY=0 NormalZ=1 Radius=11
  constraints (14):
    c: PointOnObject(g0,g-2)
    c: PointOnObject(g1,g-2)
    c: PointOnObject(g2,g-1)
    c: PointOnObject(g3,g-1)
    c: Coincident(g4,g-1)
    c: PointOnObject(g0,g4)
    c: PointOnObject(g3,g4)
    c: PointOnObject(g1,g4)
    c: PointOnObject(g2,g4)
    c: Radius(g2) = 2
    c: Equal(g2,g1)
    c: Equal(g2,g3)
    c: Equal(g2,g0)
    c: Radius(g4) = 11
FEATURE [PartDesign::Pad] Pad007
  Length = 3
  Length2 = 100
  Placement = pos=(4,0,0) rot=(0.57735,0.57735,0.57735;2.0944rad)
  Sketch = -> Sketch012
  Type = 0
FEATURE [Sketcher::SketchObject] Sketch013
  Placement = pos=(0,0,0) rot=(0.57735,0.57735,0.57735;2.0944rad)
  sketch-geometry (2):
    g0: Circle CenterX=0 CenterY=0 CenterZ=0 NormalX=0 NormalY=0 NormalZ=1 Radius=14
    g1: Circle CenterX=0 CenterY=0 CenterZ=0 NormalX=0 NormalY=0 NormalZ=1 Radius=25
  constraints (4):
    c: Coincident(g0,g-1)
    c: Coincident(g1,g-1)
    c: Radius(g0) = 14
    c: Radius(g1) = 25
FEATURE [PartDesign::Pad] Pad008  label="SurfaceCutout"
  Length = 5
  Length2 = 100
  Placement = pos=(0,0,0) rot=(0.57735,0.57735,0.57735;2.0944rad)
  Sketch = -> Sketch013
  Type = 0
FEATURE [Part::Cut] Cut004
  Base = -> Cut
  Tool = -> Pad008
FEATURE [Sketcher::SketchObject] Sketch014
  Placement = pos=(0,0,0) rot=(0.57735,0.57735,0.57735;2.0944rad)
  sketch-geometry (9):
    g0: Circle CenterX=12.5 CenterY=13 CenterZ=0 NormalX=0 NormalY=0 NormalZ=1 Radius=1.5
    g1: Circle CenterX=-12.5 CenterY=13 CenterZ=0 NormalX=0 NormalY=0 NormalZ=1 Radius=1.5
    g2: ArcOfCircle CenterX=12.5 CenterY=13 CenterZ=0 NormalX=0 NormalY=0 NormalZ=1 Radius=3 StartAngle=4.46483 EndAngle=6.37458
    g3: ArcOfCircle CenterX=-12.5 CenterY=13 CenterZ=0 NormalX=0 NormalY=0 NormalZ=1 Radius=3 StartAngle=3.0502 EndAngle=4.95995
    g4: ArcOfCircle CenterX=0 CenterY=0 CenterZ=0 NormalX=0 NormalY=0 NormalZ=1 Radius=15.5 StartAngle=0.708983 EndAngle=2.43261
    g5: Circle CenterX=0 CenterY=20 CenterZ=0 NormalX=0 NormalY=0 NormalZ=1 Radius=1.5
    g6: LineSegment StartX=-15.4875 StartY=13.2738 StartZ=0 EndX=-10 EndY=73.1515 EndZ=0
    g7: LineSegment StartX=-10 StartY=73.1515 StartZ=0 EndX=10 EndY=73.1515 EndZ=0
    g8: LineSegment StartX=10 StartY=73.1515 StartZ=0 EndX=15.4875 EndY=13.2738 EndZ=0
  constraints (25):
    c: Radius(g1) = 1.5
    c: Equal(g1,g0)
    c: Symmetric(g0,g1,g-2)
    c: DistanceX(g1,g0) = 25
    c: Coincident(g2,g0)
    c: Coincident(g3,g1)
    c: Coincident(g4,g-1)
    c: Radius(g2) = 3
    c: Equal(g2,g3)
    c: Radius(g4) = 15.5
    c: Symmetric(g4,g4,g-2)
    c: DistanceY(g-1,g1) = 13
    c: PointOnObject(g5,g-2)
    c: Equal(g5,g0)
    c: DistanceY(g-1,g5) = 20
    c: Coincident(g3,g4)
    c: Coincident(g4,g2)
    c: Coincident(g6,g7)
    c: Coincident(g7,g8)
    c: Coincident(g2,g8)
    c: Tangent(g8,g2)
    c: Coincident(g6,g3)
    c: Tangent(g3,g6)
    c: Symmetric(g6,g7,g-2)
    c: DistanceX(g7,g7) = 20
FEATURE [PartDesign::Pad] Pad009
  Length = 4
  Length2 = 100
  Placement = pos=(0,0,0) rot=(0.57735,0.57735,0.57735;2.0944rad)
  Sketch = -> Sketch014
  Type = 0
